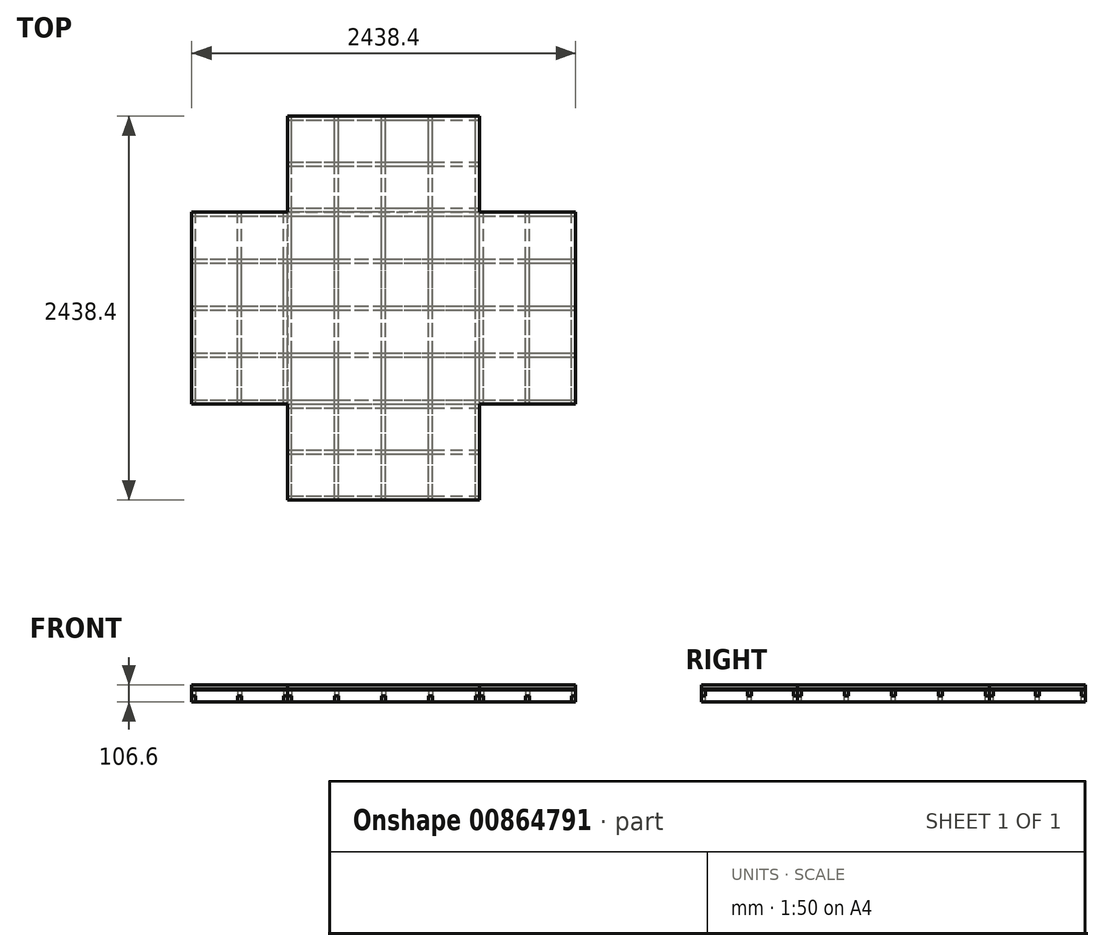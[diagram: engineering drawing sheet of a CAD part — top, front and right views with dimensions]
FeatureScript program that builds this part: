
annotation { "Feature Type Name" : "Feature", "Feature Type Description" : "" }
export const myFeature = defineFeature(function(context is Context, id is Id, definition is map)
    precondition{}
    {
        {
            var Q0;
            Q0=qCreatedBy(makeId("Top.planeOp"),FACE);
            var sketch = newSketch(context, id + "F0", { "sketchPlane" : qUnion([Q0])});
            skLineSegment(sketch, "E0.bottom", {"start": v(609.6, 609.6) * mm, "end": v(-609.6, 609.6) * mm, "construction": true});
            skLineSegment(sketch, "E0.top", {"start": v(609.6, -609.6) * mm, "end": v(-609.6, -609.6) * mm, "construction": true});
            skLineSegment(sketch, "E0.left", {"start": v(609.6, 609.6) * mm, "end": v(609.6, -609.6) * mm, "construction": true});
            skLineSegment(sketch, "E0.right", {"start": v(-609.6, 609.6) * mm, "end": v(-609.6, -609.6) * mm, "construction": true});
            skPoint(sketch, "E0.middle", {"position": v(0, 0) * mm});
            skLineSegment(sketch, "E1", {"start": v(0, 609.6) * mm, "end": v(0, -609.6) * mm, "construction": true});
            skSolve(sketch);
        }
        {
            var Q0;
            Q0=qCreatedBy(makeId("Top.planeOp"),FACE);
            var sketch = newSketch(context, id + "F1", { "sketchPlane" : qUnion([Q0])});
            skLineSegment(sketch, "E2.bottom", {"start": v(609.6, 609.6) * mm, "end": v(-609.6, 609.6) * mm});
            skLineSegment(sketch, "E2.top", {"start": v(609.6, -609.6) * mm, "end": v(-609.6, -609.6) * mm});
            skLineSegment(sketch, "E2.left", {"start": v(609.6, 609.6) * mm, "end": v(609.6, -609.6) * mm});
            skLineSegment(sketch, "E2.right", {"start": v(-609.6, 609.6) * mm, "end": v(-609.6, -609.6) * mm});
            skPoint(sketch, "E2.middle", {"position": v(0, 0) * mm});
            skLineSegment(sketch, "E3.bottom", {"start": v(-609.6, 609.6) * mm, "end": v(609.6, 609.6) * mm});
            skLineSegment(sketch, "E3.top", {"start": v(-609.6, 1219.2) * mm, "end": v(609.6, 1219.2) * mm});
            skLineSegment(sketch, "E3.left", {"start": v(-609.6, 609.6) * mm, "end": v(-609.6, 1219.2) * mm});
            skLineSegment(sketch, "E3.right", {"start": v(609.6, 609.6) * mm, "end": v(609.6, 1219.2) * mm});
            skPoint(sketch, "E3.middle", {"position": v(0, 914.4) * mm});
            skPoint(sketch, "E3.middle.positionSnap0", {"position": v(0, 609.6) * mm});
            skPoint(sketch, "E3.centerSnap0", {"position": v(0, 609.6) * mm});
            skLineSegment(sketch, "E4.1.0", {"start": v(-609.6, 609.6) * mm, "end": v(-1219.2, 609.6) * mm});
            skLineSegment(sketch, "E4.1.1", {"start": v(-1219.2, -609.6) * mm, "end": v(-1219.2, 609.6) * mm});
            skLineSegment(sketch, "E4.1.2", {"start": v(-609.6, -609.6) * mm, "end": v(-1219.2, -609.6) * mm});
            skLineSegment(sketch, "E4.2.0", {"start": v(-609.6, -609.6) * mm, "end": v(-609.6, -1219.2) * mm});
            skLineSegment(sketch, "E4.2.1", {"start": v(609.6, -1219.2) * mm, "end": v(-609.6, -1219.2) * mm});
            skLineSegment(sketch, "E4.2.2", {"start": v(609.6, -609.6) * mm, "end": v(609.6, -1219.2) * mm});
            skLineSegment(sketch, "E5.3.3.0", {"start": v(1219.2, 609.6) * mm, "end": v(1219.2, -609.6) * mm});
            skLineSegment(sketch, "E5.6.3.0", {"start": v(609.6, 609.6) * mm, "end": v(1219.2, 609.6) * mm});
            skLineSegment(sketch, "E5.7.3.0", {"start": v(609.6, -609.6) * mm, "end": v(1219.2, -609.6) * mm});
            skSolve(sketch);
        }
        {
            var Q0;
            Q0 = qSketchRegion(id + "F1", true);
            extrude(context, id + "F2", {"entities" : qUnion([Q0]), "depth" : 25.4 * mm, "offsetDistance" : 25.4 * mm});
        }
        {
            var Q0;
            Q0=makeQuery(id+"F2.opExtrude","CAP_FACE",FACE,{"disambiguationData":[OSD([sQuery(id+"F1.wireOp",EDGE,"E3.top"),sQuery(id+"F1.wireOp",EDGE,"E3.left"),sQuery(id+"F1.wireOp",EDGE,"E3.right"),sQuery(id+"F1.wireOp",EDGE,"E4.1.0"),sQuery(id+"F1.wireOp",EDGE,"E4.1.1"),sQuery(id+"F1.wireOp",EDGE,"E4.1.2"),sQuery(id+"F1.wireOp",EDGE,"E4.2.0"),sQuery(id+"F1.wireOp",EDGE,"E4.2.1"),sQuery(id+"F1.wireOp",EDGE,"E4.2.2"),sQuery(id+"F1.wireOp",EDGE,"E5.3.3.0"),sQuery(id+"F1.wireOp",EDGE,"E5.6.3.0"),sQuery(id+"F1.wireOp",EDGE,"E5.7.3.0")])],"isStart":true});
            extrude(context, id + "F3", {"entities" : qUnion([Q0]), "depth" : 5 * mm, "offsetDistance" : 25.4 * mm});
        }
        {
            var Q0;
            Q0=makeQuery(id+"F3.opExtrude","CAP_FACE",FACE,{"disambiguationData":[OSD([sQuery(id+"F1.wireOp",EDGE,"E3.top"),sQuery(id+"F1.wireOp",EDGE,"E3.left"),sQuery(id+"F1.wireOp",EDGE,"E3.right"),sQuery(id+"F1.wireOp",EDGE,"E4.1.0"),sQuery(id+"F1.wireOp",EDGE,"E4.1.1"),sQuery(id+"F1.wireOp",EDGE,"E4.1.2"),sQuery(id+"F1.wireOp",EDGE,"E4.2.0"),sQuery(id+"F1.wireOp",EDGE,"E4.2.1"),sQuery(id+"F1.wireOp",EDGE,"E4.2.2"),sQuery(id+"F1.wireOp",EDGE,"E5.3.3.0"),sQuery(id+"F1.wireOp",EDGE,"E5.6.3.0"),sQuery(id+"F1.wireOp",EDGE,"E5.7.3.0")])],"isStart":false});
            var sketch = newSketch(context, id + "F4", { "sketchPlane" : qUnion([Q0])});
            skLineSegment(sketch, "E6.bottom", {"start": v(-609.6, 1219.2) * mm, "end": v(-584.2, 1219.2) * mm});
            skLineSegment(sketch, "E6.top", {"start": v(-609.6, -1219.2) * mm, "end": v(-584.2, -1219.2) * mm});
            skLineSegment(sketch, "E6.left", {"start": v(-609.6, 1219.2) * mm, "end": v(-609.6, -1219.2) * mm});
            skLineSegment(sketch, "E6.right", {"start": v(-584.2, 1219.2) * mm, "end": v(-584.2, -1219.2) * mm});
            skLineSegment(sketch, "E7.1.0.0", {"start": v(-311.15, 1219.2) * mm, "end": v(-285.75, 1219.2) * mm});
            skLineSegment(sketch, "E7.1.0.1", {"start": v(-311.15, -1219.2) * mm, "end": v(-285.75, -1219.2) * mm});
            skLineSegment(sketch, "E7.1.0.2", {"start": v(-285.75, 1219.2) * mm, "end": v(-285.75, -1219.2) * mm});
            skLineSegment(sketch, "E7.1.0.3", {"start": v(-311.15, 1219.2) * mm, "end": v(-311.15, -1219.2) * mm});
            skLineSegment(sketch, "E7.2.0.0", {"start": v(-12.7, 1219.2) * mm, "end": v(12.7, 1219.2) * mm});
            skLineSegment(sketch, "E7.2.0.1", {"start": v(-12.7, -1219.2) * mm, "end": v(12.7, -1219.2) * mm});
            skLineSegment(sketch, "E7.2.0.2", {"start": v(12.7, 1219.2) * mm, "end": v(12.7, -1219.2) * mm});
            skLineSegment(sketch, "E7.2.0.3", {"start": v(-12.7, 1219.2) * mm, "end": v(-12.7, -1219.2) * mm});
            skLineSegment(sketch, "E7.direction1", {"start": v(-609.6, -1219.2) * mm, "end": v(-311.15, -1219.2) * mm, "construction": true});
            skLineSegment(sketch, "E8.0.3.0", {"start": v(285.75, 1219.2) * mm, "end": v(311.15, 1219.2) * mm});
            skLineSegment(sketch, "E8.3.3.0", {"start": v(285.75, -1219.2) * mm, "end": v(311.15, -1219.2) * mm});
            skLineSegment(sketch, "E8.6.3.0", {"start": v(311.15, 1219.2) * mm, "end": v(311.15, -1219.2) * mm});
            skLineSegment(sketch, "E8.9.3.0", {"start": v(285.75, 1219.2) * mm, "end": v(285.75, -1219.2) * mm});
            skLineSegment(sketch, "E9.0.4.0", {"start": v(584.2, 1219.2) * mm, "end": v(609.6, 1219.2) * mm});
            skLineSegment(sketch, "E9.3.4.0", {"start": v(584.2, -1219.2) * mm, "end": v(609.6, -1219.2) * mm});
            skLineSegment(sketch, "E9.6.4.0", {"start": v(609.6, 1219.2) * mm, "end": v(609.6, -1219.2) * mm});
            skLineSegment(sketch, "E9.9.4.0", {"start": v(584.2, 1219.2) * mm, "end": v(584.2, -1219.2) * mm});
            skSolve(sketch);
        }
        {
            var Q0;
            Q0=makeQuery(id+"F3.opExtrude","CAP_FACE",FACE,{"disambiguationData":[OSD([sQuery(id+"F1.wireOp",EDGE,"E3.top"),sQuery(id+"F1.wireOp",EDGE,"E3.left"),sQuery(id+"F1.wireOp",EDGE,"E3.right"),sQuery(id+"F1.wireOp",EDGE,"E4.1.0"),sQuery(id+"F1.wireOp",EDGE,"E4.1.1"),sQuery(id+"F1.wireOp",EDGE,"E4.1.2"),sQuery(id+"F1.wireOp",EDGE,"E4.2.0"),sQuery(id+"F1.wireOp",EDGE,"E4.2.1"),sQuery(id+"F1.wireOp",EDGE,"E4.2.2"),sQuery(id+"F1.wireOp",EDGE,"E5.3.3.0"),sQuery(id+"F1.wireOp",EDGE,"E5.6.3.0"),sQuery(id+"F1.wireOp",EDGE,"E5.7.3.0")])],"isStart":false});
            var sketch = newSketch(context, id + "F5", { "sketchPlane" : qUnion([Q0])});
            skLineSegment(sketch, "E10.bottom", {"start": v(-1219.2, 609.6) * mm, "end": v(-1193.8, 609.6) * mm});
            skLineSegment(sketch, "E10.top", {"start": v(-1219.2, -609.6) * mm, "end": v(-1193.8, -609.6) * mm});
            skLineSegment(sketch, "E10.left", {"start": v(-1219.2, 609.6) * mm, "end": v(-1219.2, -609.6) * mm});
            skLineSegment(sketch, "E10.right", {"start": v(-1193.8, 609.6) * mm, "end": v(-1193.8, -609.6) * mm});
            skLineSegment(sketch, "E11.1.0.0", {"start": v(-901.7, 609.6) * mm, "end": v(-901.7, -609.6) * mm});
            skLineSegment(sketch, "E11.1.0.1", {"start": v(-927.1, -609.6) * mm, "end": v(-901.7, -609.6) * mm});
            skLineSegment(sketch, "E11.1.0.2", {"start": v(-927.1, 609.6) * mm, "end": v(-927.1, -609.6) * mm});
            skLineSegment(sketch, "E11.1.0.3", {"start": v(-927.1, 609.6) * mm, "end": v(-901.7, 609.6) * mm});
            skLineSegment(sketch, "E11.2.0.0", {"start": v(-609.6, 609.6) * mm, "end": v(-609.6, -609.6) * mm});
            skLineSegment(sketch, "E11.2.0.1", {"start": v(-635, -609.6) * mm, "end": v(-609.6, -609.6) * mm});
            skLineSegment(sketch, "E11.2.0.2", {"start": v(-635, 609.6) * mm, "end": v(-635, -609.6) * mm});
            skLineSegment(sketch, "E11.2.0.3", {"start": v(-635, 609.6) * mm, "end": v(-609.6, 609.6) * mm});
            skLineSegment(sketch, "E11.direction1", {"start": v(-1219.2, -609.6) * mm, "end": v(-927.1, -609.6) * mm, "construction": true});
            skLineSegment(sketch, "E12.bottom", {"start": v(635, 609.6) * mm, "end": v(609.6, 609.6) * mm});
            skLineSegment(sketch, "E12.top", {"start": v(635, -609.6) * mm, "end": v(609.6, -609.6) * mm});
            skLineSegment(sketch, "E12.left", {"start": v(635, 609.6) * mm, "end": v(635, -609.6) * mm});
            skLineSegment(sketch, "E12.right", {"start": v(609.6, 609.6) * mm, "end": v(609.6, -609.6) * mm});
            skLineSegment(sketch, "E13.1.0.0", {"start": v(927.1, 609.6) * mm, "end": v(901.7, 609.6) * mm});
            skLineSegment(sketch, "E13.1.0.1", {"start": v(927.1, -609.6) * mm, "end": v(901.7, -609.6) * mm});
            skLineSegment(sketch, "E13.1.0.2", {"start": v(927.1, 609.6) * mm, "end": v(927.1, -609.6) * mm});
            skLineSegment(sketch, "E13.1.0.3", {"start": v(901.7, 609.6) * mm, "end": v(901.7, -609.6) * mm});
            skLineSegment(sketch, "E13.2.0.0", {"start": v(1219.2, 609.6) * mm, "end": v(1193.8, 609.6) * mm});
            skLineSegment(sketch, "E13.2.0.1", {"start": v(1219.2, -609.6) * mm, "end": v(1193.8, -609.6) * mm});
            skLineSegment(sketch, "E13.2.0.2", {"start": v(1219.2, 609.6) * mm, "end": v(1219.2, -609.6) * mm});
            skLineSegment(sketch, "E13.2.0.3", {"start": v(1193.8, 609.6) * mm, "end": v(1193.8, -609.6) * mm});
            skLineSegment(sketch, "E13.direction1", {"start": v(609.6, -609.6) * mm, "end": v(901.7, -609.6) * mm, "construction": true});
            skSolve(sketch);
        }
        {
            var Q0;
            Q0=makeQuery(id+"F3.opExtrude","CAP_FACE",FACE,{"disambiguationData":[OSD([sQuery(id+"F1.wireOp",EDGE,"E3.top"),sQuery(id+"F1.wireOp",EDGE,"E3.left"),sQuery(id+"F1.wireOp",EDGE,"E3.right"),sQuery(id+"F1.wireOp",EDGE,"E4.1.0"),sQuery(id+"F1.wireOp",EDGE,"E4.1.1"),sQuery(id+"F1.wireOp",EDGE,"E4.1.2"),sQuery(id+"F1.wireOp",EDGE,"E4.2.0"),sQuery(id+"F1.wireOp",EDGE,"E4.2.1"),sQuery(id+"F1.wireOp",EDGE,"E4.2.2"),sQuery(id+"F1.wireOp",EDGE,"E5.3.3.0"),sQuery(id+"F1.wireOp",EDGE,"E5.6.3.0"),sQuery(id+"F1.wireOp",EDGE,"E5.7.3.0")])],"isStart":false});
            var sketch = newSketch(context, id + "F6", { "sketchPlane" : qUnion([Q0])});
            skLineSegment(sketch, "E14.bottom", {"start": v(-1219.2, -609.6) * mm, "end": v(1219.2, -609.6) * mm});
            skLineSegment(sketch, "E14.top", {"start": v(-1219.2, -584.2) * mm, "end": v(1219.2, -584.2) * mm});
            skLineSegment(sketch, "E14.left", {"start": v(-1219.2, -609.6) * mm, "end": v(-1219.2, -584.2) * mm});
            skLineSegment(sketch, "E14.right", {"start": v(1219.2, -609.6) * mm, "end": v(1219.2, -584.2) * mm});
            skLineSegment(sketch, "E15.0.1.0", {"start": v(-1219.2, -311.15) * mm, "end": v(1219.2, -311.15) * mm});
            skLineSegment(sketch, "E15.0.1.1", {"start": v(-1219.2, -285.75) * mm, "end": v(1219.2, -285.75) * mm});
            skLineSegment(sketch, "E15.0.1.2", {"start": v(1219.2, -311.15) * mm, "end": v(1219.2, -285.75) * mm});
            skLineSegment(sketch, "E15.0.1.3", {"start": v(-1219.2, -311.15) * mm, "end": v(-1219.2, -285.75) * mm});
            skLineSegment(sketch, "E15.0.2.0", {"start": v(-1219.2, -12.7) * mm, "end": v(1219.2, -12.7) * mm});
            skLineSegment(sketch, "E15.0.2.1", {"start": v(-1219.2, 12.7) * mm, "end": v(1219.2, 12.7) * mm});
            skLineSegment(sketch, "E15.0.2.2", {"start": v(1219.2, -12.7) * mm, "end": v(1219.2, 12.7) * mm});
            skLineSegment(sketch, "E15.0.2.3", {"start": v(-1219.2, -12.7) * mm, "end": v(-1219.2, 12.7) * mm});
            skLineSegment(sketch, "E15.0.3.0", {"start": v(-1219.2, 285.75) * mm, "end": v(1219.2, 285.75) * mm});
            skLineSegment(sketch, "E15.0.3.1", {"start": v(-1219.2, 311.15) * mm, "end": v(1219.2, 311.15) * mm});
            skLineSegment(sketch, "E15.0.3.2", {"start": v(1219.2, 285.75) * mm, "end": v(1219.2, 311.15) * mm});
            skLineSegment(sketch, "E15.0.3.3", {"start": v(-1219.2, 285.75) * mm, "end": v(-1219.2, 311.15) * mm});
            skLineSegment(sketch, "E15.0.4.0", {"start": v(-1219.2, 584.2) * mm, "end": v(1219.2, 584.2) * mm});
            skLineSegment(sketch, "E15.0.4.1", {"start": v(-1219.2, 609.6) * mm, "end": v(1219.2, 609.6) * mm});
            skLineSegment(sketch, "E15.0.4.2", {"start": v(1219.2, 584.2) * mm, "end": v(1219.2, 609.6) * mm});
            skLineSegment(sketch, "E15.0.4.3", {"start": v(-1219.2, 584.2) * mm, "end": v(-1219.2, 609.6) * mm});
            skLineSegment(sketch, "E15.direction1", {"start": v(-1219.2, -609.6) * mm, "end": v(-1193.8, -609.6) * mm, "construction": true});
            skLineSegment(sketch, "E15.direction2", {"start": v(-1219.2, -609.6) * mm, "end": v(-1219.2, -311.15) * mm, "construction": true});
            skSolve(sketch);
        }
        {
            var Q0;
            Q0=makeQuery(id+"F3.opExtrude","CAP_FACE",FACE,{"disambiguationData":[OSD([sQuery(id+"F1.wireOp",EDGE,"E3.top"),sQuery(id+"F1.wireOp",EDGE,"E3.left"),sQuery(id+"F1.wireOp",EDGE,"E3.right"),sQuery(id+"F1.wireOp",EDGE,"E4.1.0"),sQuery(id+"F1.wireOp",EDGE,"E4.1.1"),sQuery(id+"F1.wireOp",EDGE,"E4.1.2"),sQuery(id+"F1.wireOp",EDGE,"E4.2.0"),sQuery(id+"F1.wireOp",EDGE,"E4.2.1"),sQuery(id+"F1.wireOp",EDGE,"E4.2.2"),sQuery(id+"F1.wireOp",EDGE,"E5.3.3.0"),sQuery(id+"F1.wireOp",EDGE,"E5.6.3.0"),sQuery(id+"F1.wireOp",EDGE,"E5.7.3.0")])],"isStart":false});
            var sketch = newSketch(context, id + "F7", { "sketchPlane" : qUnion([Q0])});
            skLineSegment(sketch, "E16.bottom", {"start": v(-609.6, -1193.8) * mm, "end": v(609.6, -1193.8) * mm});
            skLineSegment(sketch, "E16.top", {"start": v(-609.6, -1219.2) * mm, "end": v(609.6, -1219.2) * mm});
            skLineSegment(sketch, "E16.left", {"start": v(-609.6, -1193.8) * mm, "end": v(-609.6, -1219.2) * mm});
            skLineSegment(sketch, "E16.right", {"start": v(609.6, -1193.8) * mm, "end": v(609.6, -1219.2) * mm});
            skLineSegment(sketch, "E17.0.1.0", {"start": v(609.6, -901.7) * mm, "end": v(609.6, -927.1) * mm});
            skLineSegment(sketch, "E17.0.1.1", {"start": v(-609.6, -927.1) * mm, "end": v(609.6, -927.1) * mm});
            skLineSegment(sketch, "E17.0.1.2", {"start": v(-609.6, -901.7) * mm, "end": v(609.6, -901.7) * mm});
            skLineSegment(sketch, "E17.0.1.3", {"start": v(-609.6, -901.7) * mm, "end": v(-609.6, -927.1) * mm});
            skLineSegment(sketch, "E17.0.2.0", {"start": v(609.6, -609.6) * mm, "end": v(609.6, -635) * mm});
            skLineSegment(sketch, "E17.0.2.1", {"start": v(-609.6, -635) * mm, "end": v(609.6, -635) * mm});
            skLineSegment(sketch, "E17.0.2.2", {"start": v(-609.6, -609.6) * mm, "end": v(609.6, -609.6) * mm});
            skLineSegment(sketch, "E17.0.2.3", {"start": v(-609.6, -609.6) * mm, "end": v(-609.6, -635) * mm});
            skLineSegment(sketch, "E17.direction1", {"start": v(-609.6, -1219.2) * mm, "end": v(-584.2, -1219.2) * mm, "construction": true});
            skLineSegment(sketch, "E17.direction2", {"start": v(-609.6, -1219.2) * mm, "end": v(-609.6, -927.1) * mm, "construction": true});
            skLineSegment(sketch, "E18.bottom", {"start": v(-609.6, 609.6) * mm, "end": v(609.6, 609.6) * mm});
            skLineSegment(sketch, "E18.top", {"start": v(-609.6, 635) * mm, "end": v(609.6, 635) * mm});
            skLineSegment(sketch, "E18.left", {"start": v(-609.6, 609.6) * mm, "end": v(-609.6, 635) * mm});
            skLineSegment(sketch, "E18.right", {"start": v(609.6, 609.6) * mm, "end": v(609.6, 635) * mm});
            skLineSegment(sketch, "E19.0.1.0", {"start": v(609.6, 901.7) * mm, "end": v(609.6, 927.1) * mm});
            skLineSegment(sketch, "E19.0.1.1", {"start": v(-609.6, 901.7) * mm, "end": v(-609.6, 927.1) * mm});
            skLineSegment(sketch, "E19.0.1.2", {"start": v(-609.6, 927.1) * mm, "end": v(609.6, 927.1) * mm});
            skLineSegment(sketch, "E19.0.1.3", {"start": v(-609.6, 901.7) * mm, "end": v(609.6, 901.7) * mm});
            skLineSegment(sketch, "E19.0.2.0", {"start": v(609.6, 1193.8) * mm, "end": v(609.6, 1219.2) * mm});
            skLineSegment(sketch, "E19.0.2.1", {"start": v(-609.6, 1193.8) * mm, "end": v(-609.6, 1219.2) * mm});
            skLineSegment(sketch, "E19.0.2.2", {"start": v(-609.6, 1219.2) * mm, "end": v(609.6, 1219.2) * mm});
            skLineSegment(sketch, "E19.0.2.3", {"start": v(-609.6, 1193.8) * mm, "end": v(609.6, 1193.8) * mm});
            skLineSegment(sketch, "E19.direction1", {"start": v(-609.6, 609.6) * mm, "end": v(-584.2, 609.6) * mm, "construction": true});
            skLineSegment(sketch, "E19.direction2", {"start": v(-609.6, 609.6) * mm, "end": v(-609.6, 901.7) * mm, "construction": true});
            skSolve(sketch);
        }
        {
            var Q0;
            Q0 = qSketchRegion(id + "F4", true);
            extrude(context, id + "F8", {"entities" : qUnion([Q0]), "depth" : 76.2 * mm, "offsetDistance" : 25.4 * mm});
        }
        {
            var Q0;
            Q0 = qSketchRegion(id + "F5", true);
            extrude(context, id + "F9", {"entities" : qUnion([Q0]), "depth" : 76.2 * mm, "offsetDistance" : 25.4 * mm});
        }
        {
            var Q0;
            Q0 = qSketchRegion(id + "F6", true);
            var Q1;
            Q1 = qSketchRegion(id + "F7", true);
            extrude(context, id + "F10", {"entities" : qUnion([Q0, Q1]), "operationType" : NewBodyOperationType.REMOVE, "depth" : 38.1 * mm, "offsetDistance" : 25.4 * mm});
        }
        {
            var Q0;
            Q0 = qSketchRegion(id + "F6", true);
            extrude(context, id + "F11", {"entities" : qUnion([Q0]), "depth" : 76.2 * mm, "offsetDistance" : 25.4 * mm});
        }
        {
            var Q0;
            Q0 = qSketchRegion(id + "F7", true);
            extrude(context, id + "F12", {"entities" : qUnion([Q0]), "depth" : 76.2 * mm, "offsetDistance" : 25.4 * mm});
        }
        {
            var Q0;
            Q0=makeQuery(id+"F9.opExtrude","SWEPT_BODY",BODY,{"disambiguationData":[OSD([sQuery(id+"F5.wireOp",EDGE,"E13.2.0.0"),sQuery(id+"F5.wireOp",EDGE,"E13.2.0.1"),sQuery(id+"F5.wireOp",EDGE,"E13.2.0.2"),sQuery(id+"F5.wireOp",EDGE,"E13.2.0.3")])]});
            var Q1;
            Q1=makeQuery(id+"F9.opExtrude","SWEPT_BODY",BODY,{"disambiguationData":[OSD([sQuery(id+"F5.wireOp",EDGE,"E13.1.0.0"),sQuery(id+"F5.wireOp",EDGE,"E13.1.0.1"),sQuery(id+"F5.wireOp",EDGE,"E13.1.0.2"),sQuery(id+"F5.wireOp",EDGE,"E13.1.0.3")])]});
            var Q2;
            Q2=makeQuery(id+"F9.opExtrude","SWEPT_BODY",BODY,{"disambiguationData":[OSD([sQuery(id+"F5.wireOp",EDGE,"E12.bottom"),sQuery(id+"F5.wireOp",EDGE,"E12.top"),sQuery(id+"F5.wireOp",EDGE,"E12.left"),sQuery(id+"F5.wireOp",EDGE,"E12.right")])]});
            var Q3;
            Q3=makeQuery(id+"F9.opExtrude","SWEPT_BODY",BODY,{"disambiguationData":[OSD([sQuery(id+"F5.wireOp",EDGE,"E11.2.0.0"),sQuery(id+"F5.wireOp",EDGE,"E11.2.0.1"),sQuery(id+"F5.wireOp",EDGE,"E11.2.0.2"),sQuery(id+"F5.wireOp",EDGE,"E11.2.0.3")])]});
            var Q4;
            Q4=makeQuery(id+"F9.opExtrude","SWEPT_BODY",BODY,{"disambiguationData":[OSD([sQuery(id+"F5.wireOp",EDGE,"E11.1.0.0"),sQuery(id+"F5.wireOp",EDGE,"E11.1.0.1"),sQuery(id+"F5.wireOp",EDGE,"E11.1.0.2"),sQuery(id+"F5.wireOp",EDGE,"E11.1.0.3")])]});
            var Q5;
            Q5=makeQuery(id+"F9.opExtrude","SWEPT_BODY",BODY,{"disambiguationData":[OSD([sQuery(id+"F5.wireOp",EDGE,"E10.bottom"),sQuery(id+"F5.wireOp",EDGE,"E10.top"),sQuery(id+"F5.wireOp",EDGE,"E10.left"),sQuery(id+"F5.wireOp",EDGE,"E10.right")])]});
            var Q6;
            Q6=makeQuery(id+"F8.opExtrude","SWEPT_BODY",BODY,{"disambiguationData":[OSD([sQuery(id+"F4.wireOp",EDGE,"E9.0.4.0"),sQuery(id+"F4.wireOp",EDGE,"E9.3.4.0"),sQuery(id+"F4.wireOp",EDGE,"E9.6.4.0"),sQuery(id+"F4.wireOp",EDGE,"E9.9.4.0")])]});
            var Q7;
            Q7=makeQuery(id+"F8.opExtrude","SWEPT_BODY",BODY,{"disambiguationData":[OSD([sQuery(id+"F4.wireOp",EDGE,"E8.0.3.0"),sQuery(id+"F4.wireOp",EDGE,"E8.3.3.0"),sQuery(id+"F4.wireOp",EDGE,"E8.6.3.0"),sQuery(id+"F4.wireOp",EDGE,"E8.9.3.0")])]});
            var Q8;
            Q8=makeQuery(id+"F8.opExtrude","SWEPT_BODY",BODY,{"disambiguationData":[OSD([sQuery(id+"F4.wireOp",EDGE,"E7.2.0.0"),sQuery(id+"F4.wireOp",EDGE,"E7.2.0.1"),sQuery(id+"F4.wireOp",EDGE,"E7.2.0.2"),sQuery(id+"F4.wireOp",EDGE,"E7.2.0.3")])]});
            var Q9;
            Q9=makeQuery(id+"F8.opExtrude","SWEPT_BODY",BODY,{"disambiguationData":[OSD([sQuery(id+"F4.wireOp",EDGE,"E7.1.0.0"),sQuery(id+"F4.wireOp",EDGE,"E7.1.0.1"),sQuery(id+"F4.wireOp",EDGE,"E7.1.0.2"),sQuery(id+"F4.wireOp",EDGE,"E7.1.0.3")])]});
            var Q10;
            Q10=makeQuery(id+"F8.opExtrude","SWEPT_BODY",BODY,{"disambiguationData":[OSD([sQuery(id+"F4.wireOp",EDGE,"E6.bottom"),sQuery(id+"F4.wireOp",EDGE,"E6.top"),sQuery(id+"F4.wireOp",EDGE,"E6.left"),sQuery(id+"F4.wireOp",EDGE,"E6.right")])]});
            var Q11;
            Q11=makeQuery(id+"F11.opExtrude","SWEPT_BODY",BODY,{"disambiguationData":[OSD([sQuery(id+"F6.wireOp",EDGE,"E14.bottom"),sQuery(id+"F6.wireOp",EDGE,"E14.top"),sQuery(id+"F6.wireOp",EDGE,"E14.left"),sQuery(id+"F6.wireOp",EDGE,"E14.right")])]});
            var Q12;
            Q12=makeQuery(id+"F11.opExtrude","SWEPT_BODY",BODY,{"disambiguationData":[OSD([sQuery(id+"F6.wireOp",EDGE,"E15.0.2.0"),sQuery(id+"F6.wireOp",EDGE,"E15.0.2.1"),sQuery(id+"F6.wireOp",EDGE,"E15.0.2.2"),sQuery(id+"F6.wireOp",EDGE,"E15.0.2.3")])]});
            var Q13;
            Q13=makeQuery(id+"F11.opExtrude","SWEPT_BODY",BODY,{"disambiguationData":[OSD([sQuery(id+"F6.wireOp",EDGE,"E15.0.1.0"),sQuery(id+"F6.wireOp",EDGE,"E15.0.1.1"),sQuery(id+"F6.wireOp",EDGE,"E15.0.1.2"),sQuery(id+"F6.wireOp",EDGE,"E15.0.1.3")])]});
            var Q14;
            Q14=makeQuery(id+"F11.opExtrude","SWEPT_BODY",BODY,{"disambiguationData":[OSD([sQuery(id+"F6.wireOp",EDGE,"E15.0.4.0"),sQuery(id+"F6.wireOp",EDGE,"E15.0.4.1"),sQuery(id+"F6.wireOp",EDGE,"E15.0.4.2"),sQuery(id+"F6.wireOp",EDGE,"E15.0.4.3")])]});
            var Q15;
            Q15=makeQuery(id+"F11.opExtrude","SWEPT_BODY",BODY,{"disambiguationData":[OSD([sQuery(id+"F6.wireOp",EDGE,"E15.0.3.0"),sQuery(id+"F6.wireOp",EDGE,"E15.0.3.1"),sQuery(id+"F6.wireOp",EDGE,"E15.0.3.2"),sQuery(id+"F6.wireOp",EDGE,"E15.0.3.3")])]});
            var Q16;
            Q16=makeQuery(id+"F12.opExtrude","SWEPT_BODY",BODY,{"disambiguationData":[OSD([sQuery(id+"F7.wireOp",EDGE,"E17.0.1.0"),sQuery(id+"F7.wireOp",EDGE,"E17.0.1.1"),sQuery(id+"F7.wireOp",EDGE,"E17.0.1.2"),sQuery(id+"F7.wireOp",EDGE,"E17.0.1.3")])]});
            var Q17;
            Q17=makeQuery(id+"F12.opExtrude","SWEPT_BODY",BODY,{"disambiguationData":[OSD([sQuery(id+"F7.wireOp",EDGE,"E16.bottom"),sQuery(id+"F7.wireOp",EDGE,"E16.top"),sQuery(id+"F7.wireOp",EDGE,"E16.left"),sQuery(id+"F7.wireOp",EDGE,"E16.right")])]});
            var Q18;
            Q18=makeQuery(id+"F12.opExtrude","SWEPT_BODY",BODY,{"disambiguationData":[OSD([sQuery(id+"F7.wireOp",EDGE,"E18.bottom"),sQuery(id+"F7.wireOp",EDGE,"E18.top"),sQuery(id+"F7.wireOp",EDGE,"E18.left"),sQuery(id+"F7.wireOp",EDGE,"E18.right")])]});
            var Q19;
            Q19=makeQuery(id+"F12.opExtrude","SWEPT_BODY",BODY,{"disambiguationData":[OSD([sQuery(id+"F7.wireOp",EDGE,"E19.0.2.0"),sQuery(id+"F7.wireOp",EDGE,"E19.0.2.1"),sQuery(id+"F7.wireOp",EDGE,"E19.0.2.2"),sQuery(id+"F7.wireOp",EDGE,"E19.0.2.3")])]});
            var Q20;
            Q20=makeQuery(id+"F12.opExtrude","SWEPT_BODY",BODY,{"disambiguationData":[OSD([sQuery(id+"F7.wireOp",EDGE,"E19.0.1.0"),sQuery(id+"F7.wireOp",EDGE,"E19.0.1.1"),sQuery(id+"F7.wireOp",EDGE,"E19.0.1.2"),sQuery(id+"F7.wireOp",EDGE,"E19.0.1.3")])]});
            var Q21;
            Q21=makeQuery(id+"F12.opExtrude","SWEPT_BODY",BODY,{"disambiguationData":[OSD([sQuery(id+"F7.wireOp",EDGE,"E17.0.2.0"),sQuery(id+"F7.wireOp",EDGE,"E17.0.2.1"),sQuery(id+"F7.wireOp",EDGE,"E17.0.2.2"),sQuery(id+"F7.wireOp",EDGE,"E17.0.2.3")])]});
            booleanBodies(context, id + "F13", {"operationType" : BooleanOperationType.SUBTRACTION, "tools" : qUnion([Q0, Q1, Q2, Q3, Q4, Q5, Q6, Q7, Q8, Q9, Q10]), "targets" : qUnion([Q11, Q12, Q13, Q14, Q15, Q16, Q17, Q18, Q19, Q20, Q21]), "keepTools" : true});
        }
    });
